# Revit family: DAL_A3-AGI-Sliding-Patio-With-Side-Panels-(4-Panels)-3600mm
name_source: partatom
category: Doors
revit_build: Autodesk Revit 2016 (Build: 20150220_1215(x64)
units: mm (PartAtom-declared; Revit-internal decimal feet)

## family parameters
Always vertical = Yes
Cut with Voids When Loaded = No
Host = Wall
Room Calculation Point = No
Shared = No

## types (1)
- AGI sliding patio with side panels (4 panels) 3600mm
    Frame Projection Ext. = 25 mm  [stored 0.082021 ft]
    Frame Projection Int. = 25 mm  [stored 0.082021 ft]
    Frame Width = 75 mm  [stored 0.246063 ft]
    Frame material = <By Category>
    Function = Interior
    Height = 2000 mm  [stored 6.56168 ft]
    Manufacturer = AGI
    Panel 1 Width = 900 mm  [stored 2.95276 ft]
    Panel 1 heigth = 1911 mm  [stored 6.26969 ft]
    Panel 2 Hieght = 1846 mm  [stored 6.05643 ft]
    Panel 2 Width = 910 mm
    URL = http://www.agi.co.za
    Wall Closure = By host
    Width = 3600 mm  [stored 11.811 ft]

note: [stored X ft] marks values corroborated as IEEE doubles in the binary element streams (Revit-internal decimal feet)

## geometry (parser evidence)
native form markers: Sweep x17
no freeform markers — native parametric forms only
